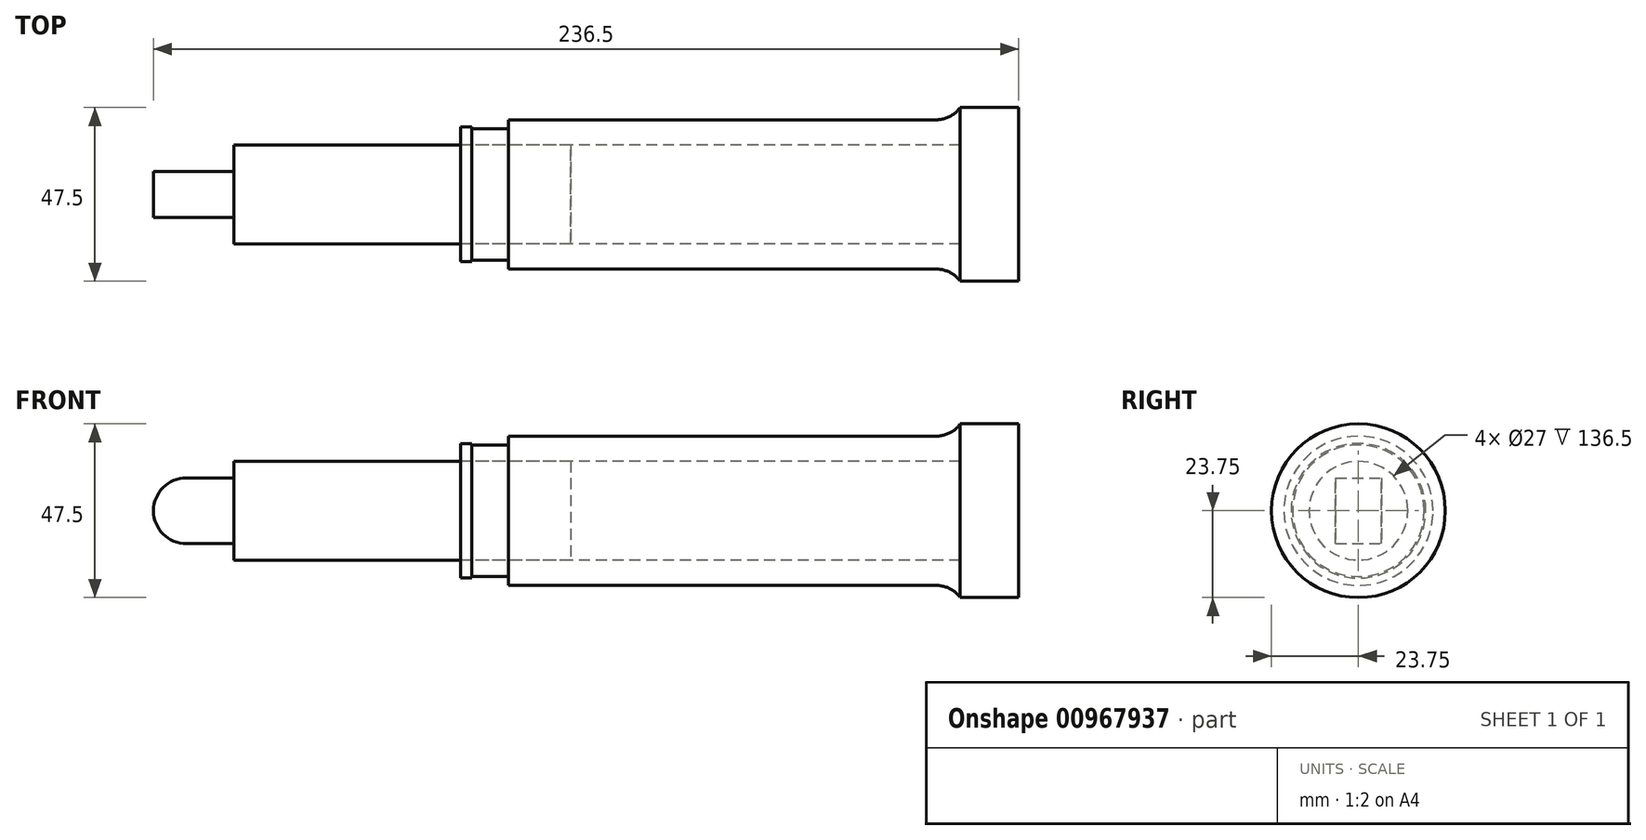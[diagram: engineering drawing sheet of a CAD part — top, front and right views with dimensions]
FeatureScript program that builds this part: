
annotation { "Feature Type Name" : "Feature", "Feature Type Description" : "" }
export const myFeature = defineFeature(function(context is Context, id is Id, definition is map)
    precondition{}
    {
        {
            var Q0;
            Q0=qCreatedBy(makeId("Front.planeOp"),FACE);
            var sketch = newSketch(context, id + "F0", { "sketchPlane" : qUnion([Q0])});
            skLineSegment(sketch, "E0", {"start": v(-88, 0) * mm, "end": v(162, 0) * mm});
            skCircle(sketch, "E1", {"center": v(-88, 0) * mm, "radius": 9 * mm});
            skCircle(sketch, "E2", {"center": v(162, 0) * mm, "radius": 9 * mm});
            skLineSegment(sketch, "E3", {"start": v(-88, 9) * mm, "end": v(-75, 9) * mm});
            skLineSegment(sketch, "E4", {"start": v(162, 9) * mm, "end": v(139.5, 9) * mm});
            skLineSegment(sketch, "E5.MirrorCS", {"start": v(-88, -9) * mm, "end": v(-75, -9) * mm});
            skLineSegment(sketch, "E6.MirrorCS", {"start": v(162, -9) * mm, "end": v(139.5, -9) * mm});
            skLineSegment(sketch, "E7", {"start": v(-75, -9) * mm, "end": v(-75, 13.5) * mm});
            skLineSegment(sketch, "E8", {"start": v(-75, 13.5) * mm, "end": v(123.5, 13.5) * mm});
            skLineSegment(sketch, "E9", {"start": v(123.5, 13.5) * mm, "end": v(123.5, 0) * mm});
            skLineSegment(sketch, "E10", {"start": v(139.5, -9) * mm, "end": v(139.5, 23.75) * mm});
            skLineSegment(sketch, "E11", {"start": v(139.5, 23.75) * mm, "end": v(123.5, 23.75) * mm});
            skLineSegment(sketch, "E12", {"start": v(0, 18) * mm, "end": v(-10, 18) * mm});
            skLineSegment(sketch, "E13", {"start": v(-10, 18.4) * mm, "end": v(-10, 18) * mm});
            skLineSegment(sketch, "E14", {"start": v(-10, 18.4) * mm, "end": v(-13, 18.4) * mm});
            skLineSegment(sketch, "E15", {"start": v(-13, 18.4) * mm, "end": v(-13, 0) * mm});
            skLineSegment(sketch, "E16", {"start": v(0, 18) * mm, "end": v(0, 20.41) * mm});
            skLineSegment(sketch, "E17", {"start": v(0, 20.41) * mm, "end": v(117, 20.41) * mm});
            skLineSegment(sketch, "E18", {"start": v(17, 13.5) * mm, "end": v(17, 0) * mm});
            skArc(sketch, "E19", {"start": v(117, 20.41) * mm, "mid": v(120.65, 21.3) * mm, "end": v(123.5, 23.75) * mm});
            skSolve(sketch);
        }
        {
            var Q0;
            {var subQ1=sQuery(id+"F0.wireOp",EDGE,"E9");Q0=makeQuery(id+"F0.imprint","IMPRINT",FACE,{"disambiguationData":[TD([[makeQuery(id+"F0.imprint","IMPRINT",EDGE,{"derivedFrom":subQ1}),1.0]])]});}
            var Q1;
            Q1=sQuery(id+"F0.wireOp",EDGE,"E0");
            revolve(context, id + "F1", {"surfaceOperationType" : NewSurfaceOperationType.NEW, "entities" : qUnion([Q0]), "axis" : qUnion([Q1]), "revolveType" : RevolveType.FULL});
        }
        {
            var Q0;
            {var subQ3=sQuery(id+"F0.wireOp",EDGE,"E15");var subQ6=sQuery(id+"F0.wireOp",EDGE,"E0");var subQ8=makeQuery(id+"F0.imprint","INTERSECT",VERTEX,{"derivedFrom":[subQ6,subQ3]});Q0=makeQuery(id+"F0.imprint","IMPRINT",FACE,{"disambiguationData":[TD([[makeQuery(id+"F0.imprint","IMPRINT",EDGE,{"disambiguationData":[TD([[subQ8,1.0]])],"derivedFrom":subQ6}),1.0]])]});}
            var Q1;
            {var subQ3=sQuery(id+"F0.wireOp",EDGE,"E18");Q1=makeQuery(id+"F0.imprint","IMPRINT",FACE,{"disambiguationData":[TD([[makeQuery(id+"F0.imprint","IMPRINT",EDGE,{"derivedFrom":subQ3}),-1.0]])]});}
            var Q2;
            Q2=sQuery(id+"F0.wireOp",EDGE,"E0");
            revolve(context, id + "F2", {"surfaceOperationType" : NewSurfaceOperationType.NEW, "entities" : qUnion([Q0, Q1]), "axis" : qUnion([Q2]), "revolveType" : RevolveType.FULL});
        }
        {
            var Q0;
            {var subQ5=sQuery(id+"F0.wireOp",EDGE,"E3");Q0=makeQuery(id+"F0.imprint","IMPRINT",FACE,{"disambiguationData":[TD([[makeQuery(id+"F0.imprint","IMPRINT",EDGE,{"derivedFrom":subQ5}),-1.0]])]});}
            var Q1;
            {var subQ5=sQuery(id+"F0.wireOp",EDGE,"E5.MirrorCS");Q1=makeQuery(id+"F0.imprint","IMPRINT",FACE,{"disambiguationData":[TD([[makeQuery(id+"F0.imprint","IMPRINT",EDGE,{"derivedFrom":subQ5}),1.0]])]});}
            var Q2;
            {var subQ0=sQuery(id+"F0.wireOp",EDGE,"E1");var subQ1=makeQuery(id+"F0.imprint","INTERSECT",VERTEX,{"derivedFrom":[subQ0,sQuery(id+"F0.wireOp",EDGE,"E3")]});Q2=makeQuery(id+"F0.imprint","IMPRINT",FACE,{"disambiguationData":[TD([[makeQuery(id+"F0.imprint","IMPRINT",EDGE,{"disambiguationData":[TD([[subQ1,1.0]])],"derivedFrom":subQ0}),1.0]])]});}
            extrude(context, id + "F3", {"entities" : qUnion([Q0, Q1, Q2]), "operationType" : NewBodyOperationType.ADD, "endBound" : BoundingType.SYMMETRIC, "depth" : 12.5 * mm, "offsetDistance" : 25 * mm});
        }
    });
